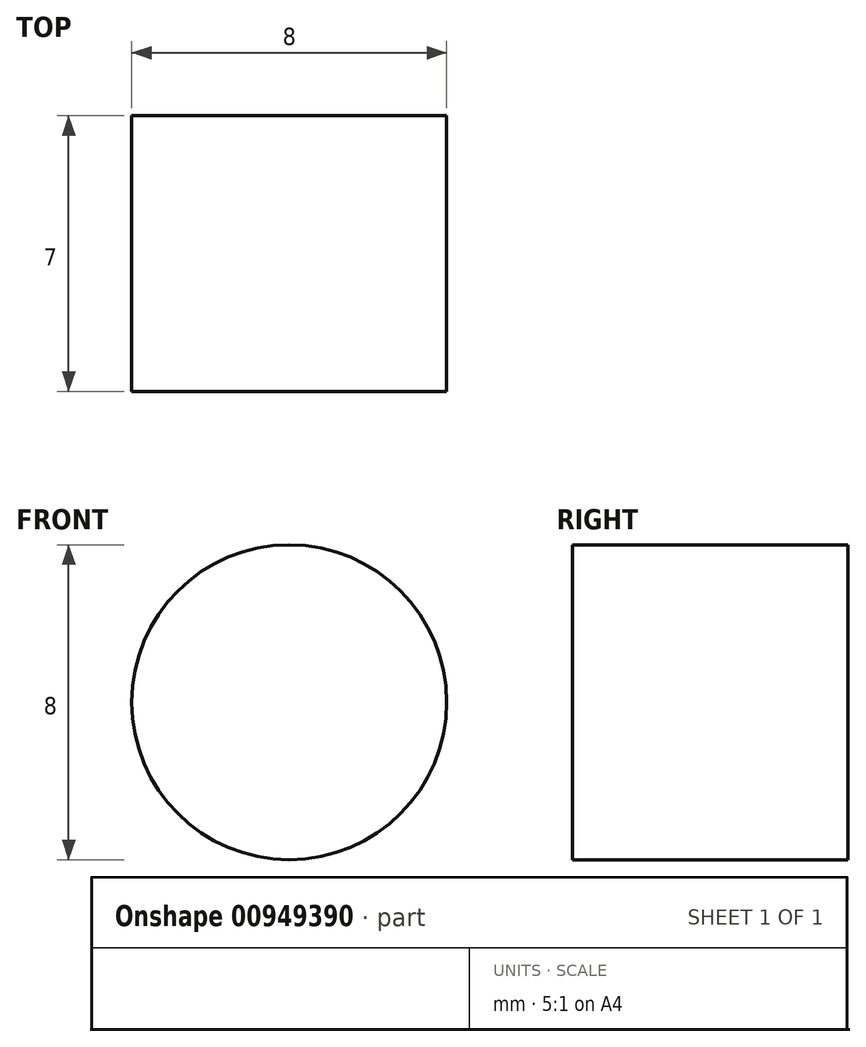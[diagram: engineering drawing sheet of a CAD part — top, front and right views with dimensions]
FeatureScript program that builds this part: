
annotation { "Feature Type Name" : "Feature", "Feature Type Description" : "" }
export const myFeature = defineFeature(function(context is Context, id is Id, definition is map)
    precondition{}
    {
        {
            var Q0;
            Q0=qCreatedBy(makeId("Front.planeOp"),FACE);
            var sketch = newSketch(context, id + "F0", { "sketchPlane" : qUnion([Q0])});
            skCircle(sketch, "E0", {"center": v(0, 0) * mm, "radius": 4 * mm});
            skSolve(sketch);
        }
        {
            var Q0;
            Q0=makeQuery(id+"F0.imprint","IMPRINT",FACE,{"disambiguationData":[TD([[makeQuery(id+"F0.imprint","IMPRINT",EDGE,{"derivedFrom":sQuery(id+"F0.wireOp",EDGE,"E0")}),1.0]])]});
            extrude(context, id + "F1", {"entities" : qUnion([Q0]), "depth" : 7 * mm, "offsetDistance" : 25 * mm});
        }
    });
